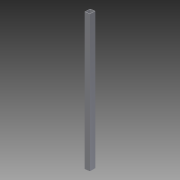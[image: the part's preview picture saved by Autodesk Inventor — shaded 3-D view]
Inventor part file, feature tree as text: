
AUTODESK INVENTOR PART (.ipt)
format: ipt  version: 2013 (Build 170138000, 138)  size: 92,672 bytes
history: native  units: in
note: dims shown in document units (in); Inventor stores cm internally (conversion verified against a paired STEP export)
features: extrude x2, sketch x2
ambient origin geometry x8: Origin, YZ Plane, XZ Plane, XY Plane, X Axis, Y Axis, Z Axis, Center Point
bodies: Solid1 (feature_tree)
feature tree (4):
  extrude  "Extrusion1"  Depth=1.0in
  extrude  "Extrusion2"  Depth=35.0in TaperAngle=0.0deg
  sketch  "Sketch1"  dims[d0=1.0in d2=1.0in]
  sketch  "Sketch2"  dims[d3=0.0625in d4=35.0in d5=0.0in d6=23.5in d8=35.0in d9=0.0in d10=23.7776in]
